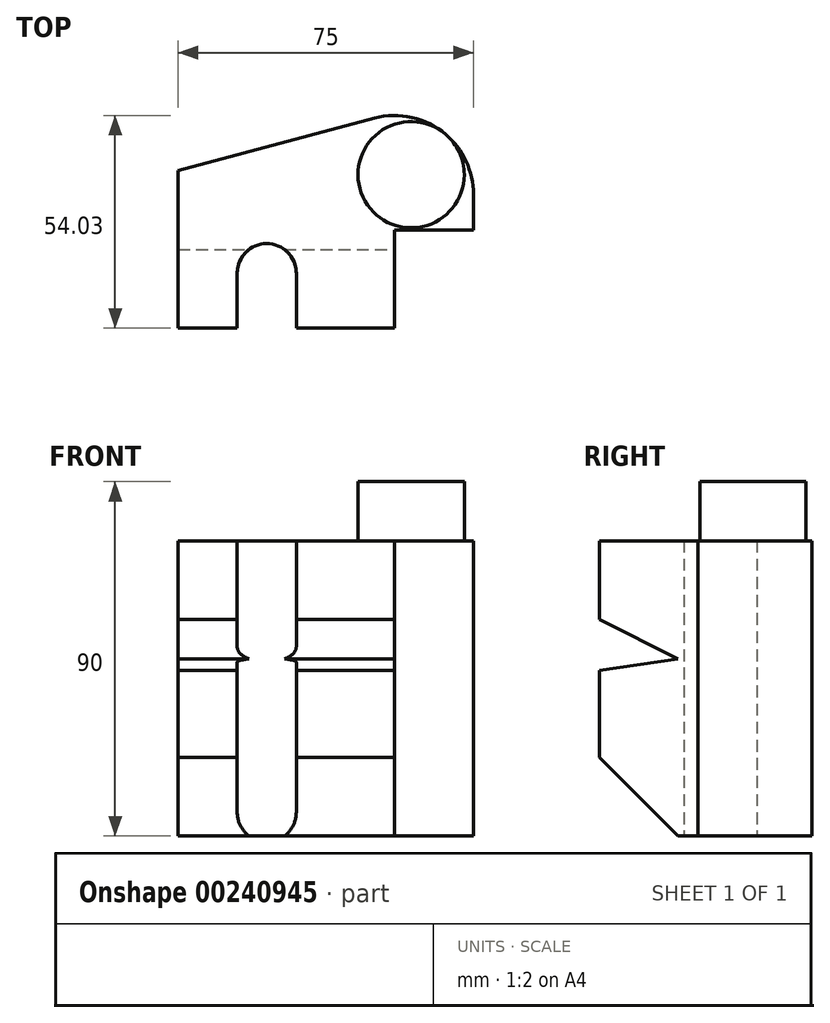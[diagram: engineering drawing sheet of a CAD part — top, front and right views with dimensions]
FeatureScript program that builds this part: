
annotation { "Feature Type Name" : "Feature", "Feature Type Description" : "" }
export const myFeature = defineFeature(function(context is Context, id is Id, definition is map)
    precondition{}
    {
        {
            var Q0;
            Q0=qCreatedBy(makeId("Top.planeOp"),FACE);
            var sketch = newSketch(context, id + "F0", { "sketchPlane" : qUnion([Q0])});
            skLineSegment(sketch, "E0", {"start": v(0, 0) * mm, "end": v(0, 40) * mm});
            skLineSegment(sketch, "E1", {"start": v(0, 40) * mm, "end": v(49.82, 53.35) * mm});
            skLineSegment(sketch, "E2", {"start": v(75, 34.03) * mm, "end": v(75, 25) * mm});
            skLineSegment(sketch, "E3", {"start": v(75, 25) * mm, "end": v(55, 25) * mm});
            skLineSegment(sketch, "E4", {"start": v(55, 25) * mm, "end": v(55, 0) * mm});
            skLineSegment(sketch, "E5", {"start": v(55, 0) * mm, "end": v(30, 0) * mm});
            skLineSegment(sketch, "E6", {"start": v(30, 0) * mm, "end": v(30, 14) * mm});
            skArc(sketch, "E7", {"start": v(30, 14) * mm, "mid": v(22.5, 21.5) * mm, "end": v(15, 14) * mm});
            skLineSegment(sketch, "E8", {"start": v(15, 14) * mm, "end": v(15, 0) * mm});
            skLineSegment(sketch, "E9", {"start": v(15, 0) * mm, "end": v(0, 0) * mm});
            skPoint(sketch, "E10.visualSharp", {"position": v(75, 60.1) * mm});
            skArc(sketch, "E10.filletArc", {"start": v(75, 34.03) * mm, "mid": v(67.18, 49.9) * mm, "end": v(49.82, 53.35) * mm});
            skSolve(sketch);
        }
        {
            var Q0;
            Q0 = qSketchRegion(id + "F0", true);
            extrude(context, id + "F1", {"entities" : qUnion([Q0]), "depth" : 75 * mm});
        }
        {
            var Q0;
            Q0=makeQuery(id+"F1.opExtrude","SWEPT_FACE",FACE,{"disambiguationData":[OSD([sQuery(id+"F0.wireOp",EDGE,"E4")])]});
            var sketch = newSketch(context, id + "F2", { "sketchPlane" : qUnion([Q0])});
            skLineSegment(sketch, "E11", {"start": v(0, 55) * mm, "end": v(20, 45) * mm});
            skLineSegment(sketch, "E12", {"start": v(20, 45) * mm, "end": v(0, 42.03) * mm});
            skLineSegment(sketch, "E13", {"start": v(0, 42.03) * mm, "end": v(0, 20) * mm});
            skLineSegment(sketch, "E14", {"start": v(0, 20) * mm, "end": v(20, 0) * mm});
            skLineSegment(sketch, "E15", {"start": v(20, 0) * mm, "end": v(0, 0) * mm});
            skLineSegment(sketch, "E16", {"start": v(0, 55) * mm, "end": v(0, 42.03) * mm});
            skLineSegment(sketch, "E17", {"start": v(0, 20) * mm, "end": v(0, 0) * mm});
            skSolve(sketch);
        }
        {
            var Q0;
            Q0 = qSketchRegion(id + "F2", true);
            extrude(context, id + "F3", {"entities" : qUnion([Q0]), "operationType" : NewBodyOperationType.REMOVE, "endBound" : BoundingType.THROUGH_ALL, "oppositeDirection" : true, "depth" : 28 * mm});
        }
        {
            var Q0;
            Q0=makeQuery(id+"F1.opExtrude","CAP_FACE",FACE,{"disambiguationData":[OSD([sQuery(id+"F0.wireOp",EDGE,"E0"),sQuery(id+"F0.wireOp",EDGE,"E1"),sQuery(id+"F0.wireOp",EDGE,"E2"),sQuery(id+"F0.wireOp",EDGE,"E3"),sQuery(id+"F0.wireOp",EDGE,"E4"),sQuery(id+"F0.wireOp",EDGE,"E5"),sQuery(id+"F0.wireOp",EDGE,"E6"),sQuery(id+"F0.wireOp",EDGE,"E7"),sQuery(id+"F0.wireOp",EDGE,"E8"),sQuery(id+"F0.wireOp",EDGE,"E9"),sQuery(id+"F0.wireOp",EDGE,"E10.filletArc")])],"isStart":false});
            var sketch = newSketch(context, id + "F4", { "sketchPlane" : qUnion([Q0])});
            skCircle(sketch, "E18", {"center": v(59.2, 39) * mm, "radius": 13.5 * mm});
            skSolve(sketch);
        }
        {
            var Q0;
            Q0 = qSketchRegion(id + "F4", true);
            extrude(context, id + "F5", {"entities" : qUnion([Q0]), "operationType" : NewBodyOperationType.ADD, "depth" : 15 * mm});
        }
    });
